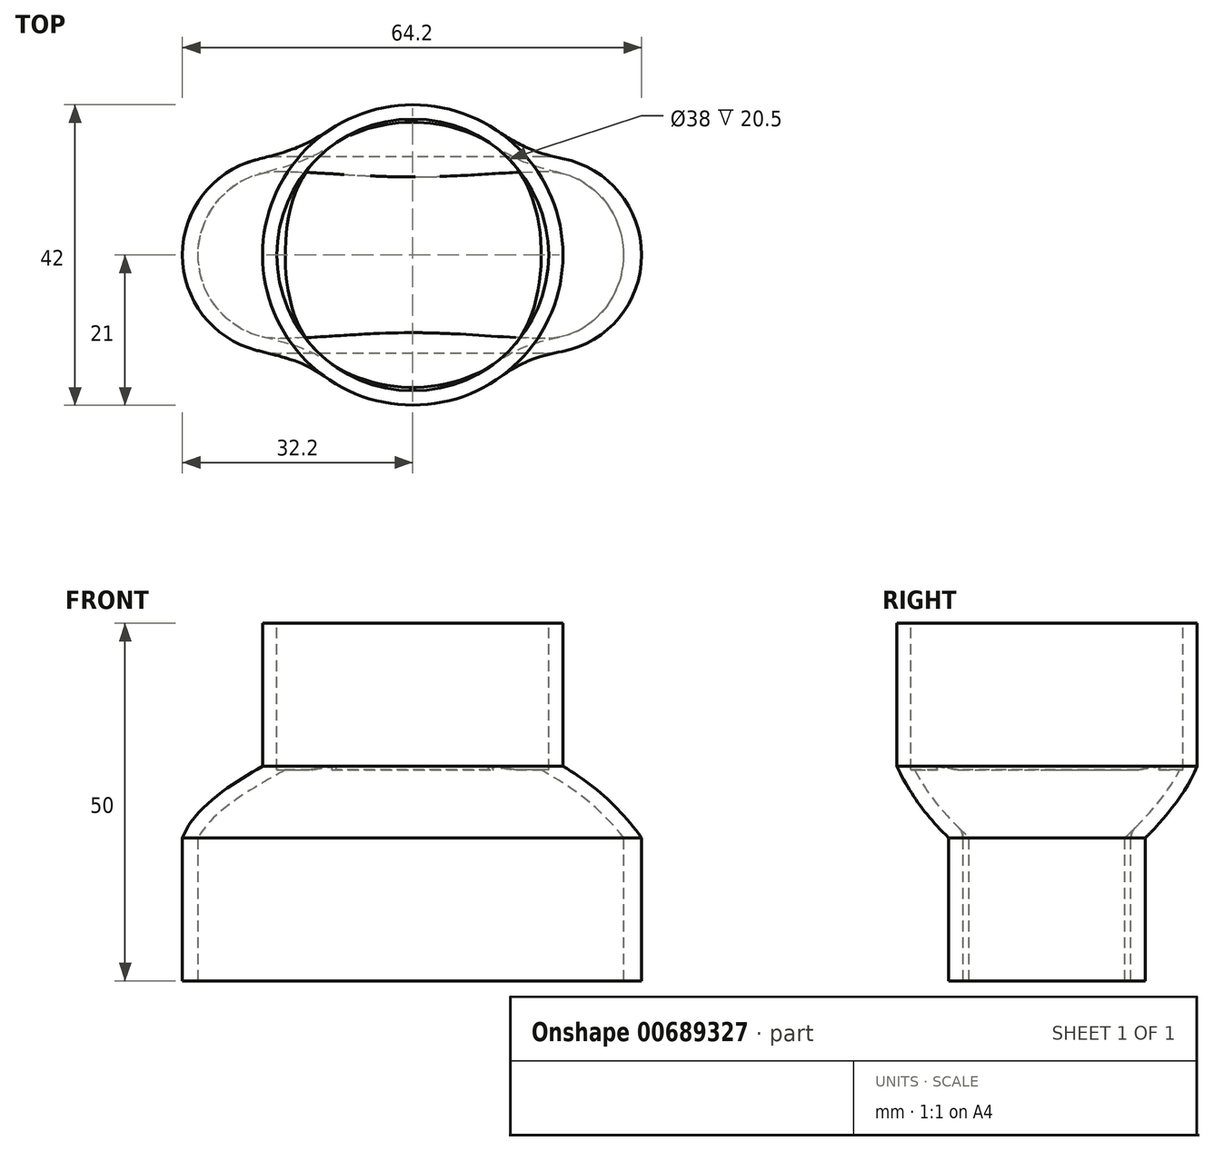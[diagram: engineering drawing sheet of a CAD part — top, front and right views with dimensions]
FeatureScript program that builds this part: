
annotation { "Feature Type Name" : "Feature", "Feature Type Description" : "" }
export const myFeature = defineFeature(function(context is Context, id is Id, definition is map)
    precondition{}
    {
        {
            var Q0;
            Q0=qCreatedBy(makeId("Top.planeOp"),FACE);
            var sketch = newSketch(context, id + "F0", { "sketchPlane" : qUnion([Q0])});
            skPoint(sketch, "E0.middle", {"position": v(0, 0) * mm});
            skLineSegment(sketch, "E1.bottom", {"start": v(18.25, -13.75) * mm, "end": v(-18.45, -13.75) * mm});
            skLineSegment(sketch, "E1.top", {"start": v(18.25, 13.75) * mm, "end": v(-18.45, 13.75) * mm});
            skArc(sketch, "E2", {"start": v(18.25, -13.75) * mm, "mid": v(32, 0) * mm, "end": v(18.25, 13.75) * mm});
            skArc(sketch, "E3", {"start": v(-18.45, 13.75) * mm, "mid": v(-32.2, 0) * mm, "end": v(-18.45, -13.75) * mm});
            skLineSegment(sketch, "E4", {"start": v(32, 13.75) * mm, "end": v(32, -13.75) * mm, "construction": true});
            skPoint(sketch, "E4.startSnap0", {"position": v(32, 0) * mm});
            skLineSegment(sketch, "E5", {"start": v(-32.2, 13.75) * mm, "end": v(-32.2, -13.75) * mm, "construction": true});
            skPoint(sketch, "E5.startSnap0", {"position": v(-32.2, 0) * mm});
            skSolve(sketch);
        }
        {
            var Q0;
            Q0=qCreatedBy(makeId("Top.planeOp"),FACE);
            cPlane(context, id + "F1", {"entities" : qUnion([Q0]), "cplaneType" : CPlaneType.OFFSET, "offset" : 10 * mm, "width" : 150 * mm, "height" : 150 * mm});
        }
        {
            var Q0;
            Q0=qCreatedBy(id+"F1.planeOp",FACE);
            var sketch = newSketch(context, id + "F2", { "sketchPlane" : qUnion([Q0])});
            skCircle(sketch, "E6", {"center": v(0, 0) * mm, "radius": 21 * mm});
            skSolve(sketch);
        }
        {
            var Q0;
            Q0=qCreatedBy(makeId("Front.planeOp"),FACE);
            var sketch = newSketch(context, id + "F3", { "sketchPlane" : qUnion([Q0])});
            skLineSegment(sketch, "E7.0", {"start": v(-21, 10) * mm, "end": v(21, 10) * mm, "construction": true});
            skLineSegment(sketch, "E8.0", {"start": v(-18.45, 0) * mm, "end": v(-32.2, 0) * mm, "construction": true});
            skLineSegment(sketch, "E9.0", {"start": v(18.25, 0) * mm, "end": v(32, 0) * mm, "construction": true});
            skFitSpline(sketch, "E10", {"points": [v(-21, 10) * mm, v(-32.2, 0) * mm], "startDerivative": vector(-13.15, -7.42) * mm, "endDerivative": vector(-4.77, -12.52) * mm});
            skFitSpline(sketch, "E11", {"points": [v(32, 0) * mm, v(21, 10) * mm], "startDerivative": vector(-10.02, 13.41) * mm, "endDerivative": vector(-14.2, 8.6) * mm});
            skSolve(sketch);
        }
        {
            var Q0;
            Q0=qCreatedBy(makeId("Right.planeOp"),FACE);
            var sketch = newSketch(context, id + "F4", { "sketchPlane" : qUnion([Q0])});
            skLineSegment(sketch, "E12.0", {"start": v(-13.75, 0) * mm, "end": v(13.75, 0) * mm, "construction": true});
            skLineSegment(sketch, "E13.0", {"start": v(-21, 10) * mm, "end": v(21, 10) * mm, "construction": true});
            skFitSpline(sketch, "E14", {"points": [v(-21, 10) * mm, v(-13.75, 0) * mm], "startDerivative": vector(5.47, -11.4) * mm, "endDerivative": vector(9.61, -9.27) * mm});
            skFitSpline(sketch, "E15", {"points": [v(21, 10) * mm, v(13.75, 0) * mm], "startDerivative": vector(-4.42, -10.5) * mm, "endDerivative": vector(-9.78, -9.72) * mm});
            skSolve(sketch);
        }
        {
            var Q0;
            Q0 = qSketchRegion(id + "F0", true);
            var Q1;
            Q1 = qSketchRegion(id + "F2", true);
            var Q2;
            Q2=sQuery(id+"F4.wireOp",EDGE,"E15");
            var Q3;
            Q3=sQuery(id+"F4.wireOp",EDGE,"E14");
            var Q4;
            Q4=sQuery(id+"F3.wireOp",EDGE,"E10");
            var Q5;
            Q5=sQuery(id+"F3.wireOp",EDGE,"E11");
            loft(context, id + "F5", {"addGuides" : true, "sheetProfilesArray" : [{ "sheetProfileEntities" : qUnion([Q0]) }, { "sheetProfileEntities" : qUnion([Q1]) }], "guidesArray" : [{ "guideEntities" : qUnion([Q2]), "guideDerivativeType" : LoftGuideDerivativeType.DEFAULT, "guideDerivativeMagnitude" : 1 }, { "guideEntities" : qUnion([Q3]), "guideDerivativeType" : LoftGuideDerivativeType.DEFAULT, "guideDerivativeMagnitude" : 1 }, { "guideEntities" : qUnion([Q4]), "guideDerivativeType" : LoftGuideDerivativeType.DEFAULT, "guideDerivativeMagnitude" : 1 }, { "guideEntities" : qUnion([Q5]), "guideDerivativeType" : LoftGuideDerivativeType.DEFAULT, "guideDerivativeMagnitude" : 1 }]});
        }
        {
            var Q0;
            Q0=makeQuery(id+"F5.opLoft","CAP_FACE",FACE,{"disambiguationData":[OSD([makeQuery(id+"F2.imprint","IMPRINT",FACE,{"disambiguationData":[TD([[makeQuery(id+"F2.imprint","IMPRINT",EDGE,{"derivedFrom":sQuery(id+"F2.wireOp",EDGE,"E6")}),1.0]])]})])],"isStart":true});
            var Q1;
            Q1=makeQuery(id+"F5.opLoft","CAP_FACE",FACE,{"disambiguationData":[OSD([makeQuery(id+"F0.imprint","IMPRINT",FACE,{"disambiguationData":[TD([[makeQuery(id+"F0.imprint","IMPRINT",EDGE,{"derivedFrom":sQuery(id+"F0.wireOp",EDGE,"E1.bottom")}),-1.0]])]})])],"isStart":true});
            shell(context, id + "F6", {"entities" : qUnion([Q0, Q1]), "thickness" : 2 * mm});
        }
        {
            var Q0;
            Q0=makeQuery(id+"F5.opLoft","CAP_FACE",FACE,{"disambiguationData":[OSD([makeQuery(id+"F0.imprint","IMPRINT",FACE,{"disambiguationData":[TD([[makeQuery(id+"F0.imprint","IMPRINT",EDGE,{"derivedFrom":sQuery(id+"F0.wireOp",EDGE,"E1.bottom")}),-1.0]])]})])],"isStart":true});
            extrude(context, id + "F7", {"entities" : qUnion([Q0]), "operationType" : NewBodyOperationType.ADD, "depth" : 20 * mm, "offsetDistance" : 25 * mm});
        }
        {
            var Q0;
            Q0=makeQuery(id+"F5.opLoft","CAP_FACE",FACE,{"disambiguationData":[OSD([makeQuery(id+"F2.imprint","IMPRINT",FACE,{"disambiguationData":[TD([[makeQuery(id+"F2.imprint","IMPRINT",EDGE,{"derivedFrom":sQuery(id+"F2.wireOp",EDGE,"E6")}),1.0]])]})])],"isStart":true});
            extrude(context, id + "F8", {"entities" : qUnion([Q0]), "operationType" : NewBodyOperationType.ADD, "depth" : 20 * mm, "offsetDistance" : 25 * mm});
        }
        {
            var Q0;
            Q0=makeQuery(id+"F8.opExtrude","CAP_FACE",FACE,{"disambiguationData":[OSD([makeQuery(id+"F2.imprint","IMPRINT",FACE,{"disambiguationData":[TD([[makeQuery(id+"F2.imprint","IMPRINT",EDGE,{"derivedFrom":sQuery(id+"F2.wireOp",EDGE,"E6")}),1.0]])]})])],"isStart":false});
            cPlane(context, id + "F9", {"entities" : qUnion([Q0]), "cplaneType" : CPlaneType.OFFSET, "offset" : 0 * mm, "width" : 150 * mm, "height" : 150 * mm});
        }
        {
            var Q0;
            Q0=qCreatedBy(id+"F9.planeOp",FACE);
            var sketch = newSketch(context, id + "F10", { "sketchPlane" : qUnion([Q0])});
            skCircle(sketch, "E16", {"center": v(0, 0) * mm, "radius": 19 * mm});
            skSolve(sketch);
        }
        {
            var Q0;
            Q0 = qSketchRegion(id + "F10", true);
            extrude(context, id + "F11", {"entities" : qUnion([Q0]), "operationType" : NewBodyOperationType.REMOVE, "oppositeDirection" : true, "depth" : 20.5 * mm, "offsetDistance" : 25 * mm});
        }
    });
